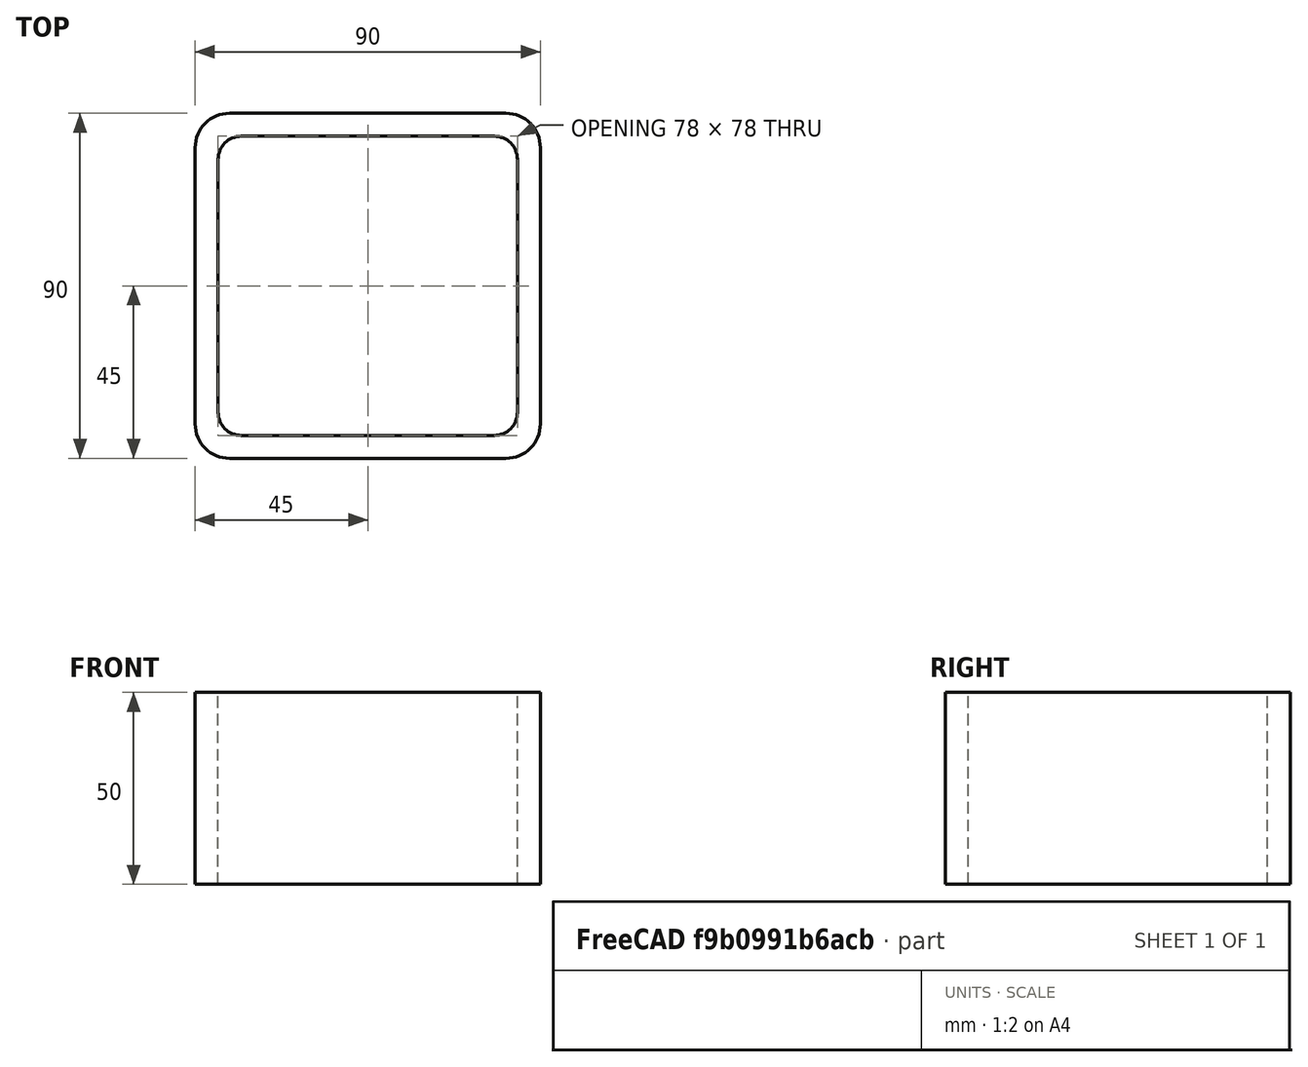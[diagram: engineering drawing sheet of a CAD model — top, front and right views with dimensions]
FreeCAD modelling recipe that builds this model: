
FCSTD DOCUMENT  (FreeCAD 0.15R4671 (Git))
Label: Square hollow section 90x90x6 EN10219 S235JRH
License: All rights reserved
LicenseURL: http://en.wikipedia.org/wiki/All_rights_reserved
objects: Sketcher::SketchObject×1, Part::Extrusion×1
note: 2 computed .brp shape members not serialized (recipe doc carries the construction recipe); baked Part::Feature solids carry a one-line shape summary decoded from their .brp

FEATURE [Sketcher::SketchObject] Sketch
  sketch-geometry (16):
    g0: LineSegment StartX=-33 StartY=39 StartZ=0 EndX=33 EndY=39 EndZ=0
    g1: LineSegment StartX=39 StartY=33 StartZ=0 EndX=39 EndY=-33 EndZ=0
    g2: LineSegment StartX=33 StartY=-39 StartZ=0 EndX=-33 EndY=-39 EndZ=0
    g3: LineSegment StartX=-39 StartY=-33 StartZ=0 EndX=-39 EndY=33 EndZ=0
    g4: LineSegment StartX=-36 StartY=45 StartZ=0 EndX=36 EndY=45 EndZ=0
    g5: LineSegment StartX=45 StartY=36 StartZ=0 EndX=45 EndY=-36 EndZ=0
    g6: LineSegment StartX=36 StartY=-45 StartZ=0 EndX=-36 EndY=-45 EndZ=0
    g7: LineSegment StartX=-45 StartY=-36 StartZ=0 EndX=-45 EndY=36 EndZ=0
    g8: ArcOfCircle CenterX=-33 CenterY=33 CenterZ=0 NormalX=0 NormalY=0 NormalZ=1 Radius=6 StartAngle=1.5708 EndAngle=3.14159
    g9: ArcOfCircle CenterX=33 CenterY=33 CenterZ=0 NormalX=0 NormalY=0 NormalZ=1 Radius=6 StartAngle=0 EndAngle=1.5708
    g10: ArcOfCircle CenterX=33 CenterY=-33 CenterZ=0 NormalX=0 NormalY=0 NormalZ=1 Radius=6 StartAngle=4.71239 EndAngle=6.28319
    g11: ArcOfCircle CenterX=-33 CenterY=-33 CenterZ=0 NormalX=0 NormalY=0 NormalZ=1 Radius=6 StartAngle=3.14159 EndAngle=4.71239
    g12: ArcOfCircle CenterX=36 CenterY=36 CenterZ=0 NormalX=0 NormalY=0 NormalZ=1 Radius=9 StartAngle=0 EndAngle=1.5708
    g13: ArcOfCircle CenterX=36 CenterY=-36 CenterZ=0 NormalX=0 NormalY=0 NormalZ=1 Radius=9 StartAngle=4.71239 EndAngle=6.28319
    g14: ArcOfCircle CenterX=-36 CenterY=-36 CenterZ=0 NormalX=0 NormalY=0 NormalZ=1 Radius=9 StartAngle=3.14159 EndAngle=4.71239
    g15: ArcOfCircle CenterX=-36 CenterY=36 CenterZ=0 NormalX=0 NormalY=0 NormalZ=1 Radius=9 StartAngle=1.5708 EndAngle=3.14159
  constraints (36):
    c: Horizontal(g2)
    c: Vertical(g3)
    c: Horizontal(g6)
    c: Vertical(g7)
    c: Tangent(g3,g8) = 1.5708
    c: Tangent(g0,g8) = 1.5708
    c: Tangent(g0,g9) = 1.5708
    c: Tangent(g1,g9) = 1.5708
    c: Tangent(g1,g10) = 1.5708
    c: Tangent(g2,g10) = 1.5708
    c: Tangent(g2,g11) = 1.5708
    c: Tangent(g3,g11) = 1.5708
    c: Tangent(g4,g12) = 1.5708
    c: Tangent(g5,g12) = 1.5708
    c: Tangent(g5,g13) = 1.5708
    c: Tangent(g6,g13) = 1.5708
    c: Tangent(g6,g14) = 1.5708
    c: Tangent(g7,g14) = 1.5708
    c: Tangent(g7,g15) = 1.5708
    c: Tangent(g4,g15) = 1.5708
    c: Equal(g9,g8)
    c: Equal(g9,g11)
    c: Equal(g9,g10)
    c: Equal(g12,g15)
    c: Equal(g12,g14)
    c: Equal(g12,g13)
    c: Symmetric(g4,g6,g-1)
    c: Symmetric(g7,g5,g-2)
    c: DistanceY(g4,g6) = -90
    c: DistanceX(g7,g5) = 90
    c: Symmetric(g3,g1,g-2)
    c: Symmetric(g0,g2,g-1)
    c: DistanceY(g0,g4) = 6
    c: DistanceX(g5,g1) = -6
    c: Radius(g9) = 6
    c: Radius(g12) = 9
FEATURE [Part::Extrusion] Extrude  label="Square hollow section 90x90x6 EN10219 S235JRH"
  Base = -> Sketch
  Dir = (0,0,50)
  Solid = true
